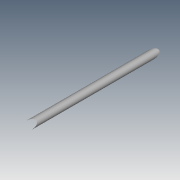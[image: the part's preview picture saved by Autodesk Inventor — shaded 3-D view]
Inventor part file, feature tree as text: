
AUTODESK INVENTOR PART (.ipt)
format: ipt  version: 2015 (Build 190159000, 159)  size: 67,584 bytes
history: native  units: mm
features: extrude x1, sketch x1
ambient origin geometry x8: Origin, YZ Plane, XZ Plane, XY Plane, X Axis, Y Axis, Z Axis, Center Point
bodies: Solid1 (feature_tree)
feature tree (2):
  extrude  "Extrusion1"  Depth=210.0mm TaperAngle=0.0deg
  sketch  "Sketch1"  dims[d0=10.0mm d1=210.0mm d2=0.0mm]
